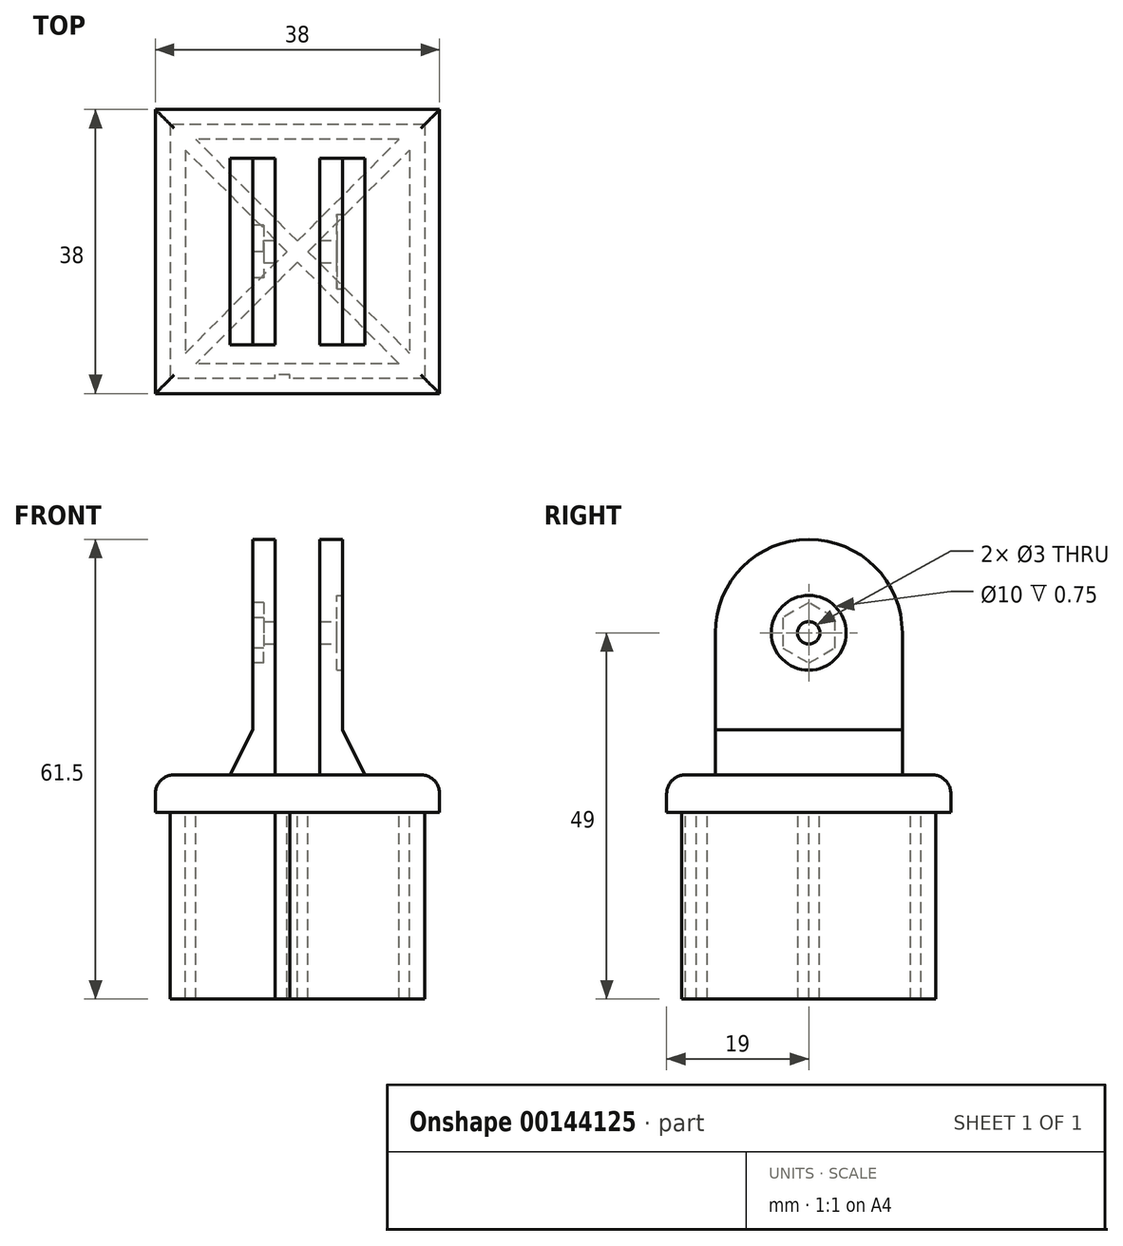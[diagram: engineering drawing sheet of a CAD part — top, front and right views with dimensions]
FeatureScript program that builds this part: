
annotation { "Feature Type Name" : "Feature", "Feature Type Description" : "" }
export const myFeature = defineFeature(function(context is Context, id is Id, definition is map)
    precondition{}
    {
        {
            var Q0;
            Q0=qCreatedBy(makeId("Top.planeOp"),FACE);
            var sketch = newSketch(context, id + "F0", { "sketchPlane" : qUnion([Q0])});
            skLineSegment(sketch, "E0.bottom", {"start": v(17, 17) * mm, "end": v(-17, 17) * mm});
            skLineSegment(sketch, "E0.top", {"start": v(17, -17) * mm, "end": v(-17, -17) * mm});
            skLineSegment(sketch, "E0.left", {"start": v(17, 17) * mm, "end": v(17, -17) * mm});
            skLineSegment(sketch, "E0.right", {"start": v(-17, 17) * mm, "end": v(-17, -17) * mm});
            skPoint(sketch, "E0.middle", {"position": v(0, 0) * mm});
            skLineSegment(sketch, "E1.bottom", {"start": v(19, 19) * mm, "end": v(-19, 19) * mm});
            skLineSegment(sketch, "E1.top", {"start": v(19, -19) * mm, "end": v(-19, -19) * mm});
            skLineSegment(sketch, "E1.left", {"start": v(19, 19) * mm, "end": v(19, -19) * mm});
            skLineSegment(sketch, "E1.right", {"start": v(-19, 19) * mm, "end": v(-19, -19) * mm});
            skLineSegment(sketch, "E2.bottom", {"start": v(15, 15) * mm, "end": v(-15, 15) * mm});
            skLineSegment(sketch, "E2.top", {"start": v(15, -15) * mm, "end": v(-15, -15) * mm});
            skLineSegment(sketch, "E2.left", {"start": v(15, 15) * mm, "end": v(15, -15) * mm});
            skLineSegment(sketch, "E2.right", {"start": v(-15, 15) * mm, "end": v(-15, -15) * mm});
            skSolve(sketch);
        }
        {
            var Q0;
            Q0 = qSketchRegion(id + "F0", true);
            var Q1;
            Q1=makeQuery(id+"F0.imprint","IMPRINT",FACE,{"disambiguationData":[TD([[makeQuery(id+"F0.imprint","IMPRINT",EDGE,{"derivedFrom":sQuery(id+"F0.wireOp",EDGE,"E0.bottom")}),1.0]])]});
            var Q2;
            Q2=makeQuery(id+"F0.imprint","IMPRINT",FACE,{"disambiguationData":[TD([[makeQuery(id+"F0.imprint","IMPRINT",EDGE,{"derivedFrom":sQuery(id+"F0.wireOp",EDGE,"E2.bottom")}),1.0]])]});
            extrude(context, id + "F1", {"entities" : qUnion([Q0, Q1, Q2]), "depth" : 5 * mm});
        }
        {
            var Q0;
            Q0=makeQuery(id+"F0.imprint","IMPRINT",FACE,{"disambiguationData":[TD([[makeQuery(id+"F0.imprint","IMPRINT",EDGE,{"derivedFrom":sQuery(id+"F0.wireOp",EDGE,"E0.bottom")}),1.0]])]});
            extrude(context, id + "F2", {"entities" : qUnion([Q0]), "operationType" : NewBodyOperationType.ADD, "oppositeDirection" : true, "depth" : 25 * mm});
        }
        {
            var Q0;
            Q0=makeQuery(id+"F0.imprint","IMPRINT",FACE,{"disambiguationData":[TD([[makeQuery(id+"F0.imprint","IMPRINT",EDGE,{"derivedFrom":sQuery(id+"F0.wireOp",EDGE,"E2.bottom")}),1.0]])]});
            var sketch = newSketch(context, id + "F3", { "sketchPlane" : qUnion([Q0])});
            skPoint(sketch, "E3", {"position": v(-15, 15) * mm});
            skPoint(sketch, "E4", {"position": v(15, -15) * mm});
            skPoint(sketch, "E5", {"position": v(-15, -15) * mm});
            skPoint(sketch, "E6", {"position": v(15, 15) * mm});
            skLineSegment(sketch, "E7", {"start": v(0.7, 0.7) * mm, "end": v(-13.59, 15) * mm});
            skLineSegment(sketch, "E8", {"start": v(-13.59, 15) * mm, "end": v(-15, 15) * mm});
            skLineSegment(sketch, "E9", {"start": v(-0.7, -0.7) * mm, "end": v(-15, 13.59) * mm});
            skLineSegment(sketch, "E10", {"start": v(-15, 13.59) * mm, "end": v(-15, 15) * mm});
            skLineSegment(sketch, "E11", {"start": v(-0.7, -0.7) * mm, "end": v(13.59, -15) * mm});
            skLineSegment(sketch, "E12", {"start": v(13.59, -15) * mm, "end": v(15, -15) * mm});
            skLineSegment(sketch, "E13", {"start": v(0.7, 0.7) * mm, "end": v(15, -13.59) * mm});
            skLineSegment(sketch, "E14", {"start": v(15, -13.59) * mm, "end": v(15, -15) * mm});
            skLineSegment(sketch, "E15", {"start": v(0, -1.41) * mm, "end": v(-13.59, -15) * mm});
            skLineSegment(sketch, "E16", {"start": v(-13.59, -15) * mm, "end": v(-15, -15) * mm});
            skLineSegment(sketch, "E17", {"start": v(-15, -13.59) * mm, "end": v(-1.41, 0) * mm});
            skLineSegment(sketch, "E18", {"start": v(1.41, 0) * mm, "end": v(15, 13.59) * mm});
            skLineSegment(sketch, "E19", {"start": v(15, 13.59) * mm, "end": v(15, 15) * mm});
            skLineSegment(sketch, "E20", {"start": v(0.7, 0.7) * mm, "end": v(0, 1.41) * mm});
            skLineSegment(sketch, "E21", {"start": v(0, 1.41) * mm, "end": v(13.59, 15) * mm});
            skLineSegment(sketch, "E22", {"start": v(13.59, 15) * mm, "end": v(15, 15) * mm});
            skSolve(sketch);
        }
        {
            var Q0;
            Q0 = qSketchRegion(id + "F3", true);
            extrude(context, id + "F4", {"entities" : qUnion([Q0]), "operationType" : NewBodyOperationType.ADD, "oppositeDirection" : true, "depth" : 25 * mm});
        }
        {
            var Q0;
            {var subQ0=sQuery(id+"F3.wireOp",EDGE,"E15");Q0=makeQuery(id+"F3.imprint","IMPRINT",FACE,{"disambiguationData":[TD([[makeQuery(id+"F3.imprint","IMPRINT",EDGE,{"derivedFrom":subQ0}),-1.0]])]});}
            extrude(context, id + "F5", {"entities" : qUnion([Q0]), "operationType" : NewBodyOperationType.ADD, "oppositeDirection" : true, "depth" : 25 * mm});
        }
        {
            var Q0;
            Q0=makeQuery(id+"F1.opExtrude","CAP_EDGE",EDGE,{"disambiguationData":[OSD([sQuery(id+"F0.wireOp",EDGE,"E1.bottom")])],"isStart":false});
            var Q1;
            Q1=makeQuery(id+"F1.opExtrude","CAP_EDGE",EDGE,{"disambiguationData":[OSD([sQuery(id+"F0.wireOp",EDGE,"E1.left")])],"isStart":false});
            var Q2;
            Q2=makeQuery(id+"F1.opExtrude","CAP_EDGE",EDGE,{"disambiguationData":[OSD([sQuery(id+"F0.wireOp",EDGE,"E1.right")])],"isStart":false});
            var Q3;
            Q3=makeQuery(id+"F1.opExtrude","CAP_EDGE",EDGE,{"disambiguationData":[OSD([sQuery(id+"F0.wireOp",EDGE,"E1.top")])],"isStart":false});
            fillet(context, id + "F6", {"entities" : qUnion([Q0, Q1, Q2, Q3]), "radius" : 2.5 * mm, "tangentPropagation" : true, "allowEdgeOverflow" : false});
        }
        {
            var Q0;
            Q0=makeQuery(id+"F1.opExtrude","CAP_FACE",FACE,{"disambiguationData":[OSD([sQuery(id+"F0.wireOp",EDGE,"E1.bottom"),sQuery(id+"F0.wireOp",EDGE,"E1.top"),sQuery(id+"F0.wireOp",EDGE,"E1.left"),sQuery(id+"F0.wireOp",EDGE,"E1.right")])],"isStart":false});
            var sketch = newSketch(context, id + "F7", { "sketchPlane" : qUnion([Q0])});
            skLineSegment(sketch, "E23.bottom", {"start": v(3, 12.5) * mm, "end": v(-3, 12.5) * mm});
            skLineSegment(sketch, "E23.top", {"start": v(3, -12.5) * mm, "end": v(-3, -12.5) * mm});
            skLineSegment(sketch, "E23.left", {"start": v(3, 12.5) * mm, "end": v(3, -12.5) * mm});
            skLineSegment(sketch, "E23.right", {"start": v(-3, 12.5) * mm, "end": v(-3, -12.5) * mm});
            skPoint(sketch, "E23.middle", {"position": v(0, 0) * mm});
            skLineSegment(sketch, "E24.bottom", {"start": v(3, 12.5) * mm, "end": v(6, 12.5) * mm});
            skLineSegment(sketch, "E24.top", {"start": v(3, -12.5) * mm, "end": v(6, -12.5) * mm});
            skLineSegment(sketch, "E24.right", {"start": v(6, 12.5) * mm, "end": v(6, -12.5) * mm});
            skLineSegment(sketch, "E25.bottom", {"start": v(-3, 12.5) * mm, "end": v(-6, 12.5) * mm});
            skLineSegment(sketch, "E25.top", {"start": v(-3, -12.5) * mm, "end": v(-6, -12.5) * mm});
            skLineSegment(sketch, "E25.right", {"start": v(-6, 12.5) * mm, "end": v(-6, -12.5) * mm});
            skLineSegment(sketch, "E26.bottom", {"start": v(6, 12.5) * mm, "end": v(9, 12.5) * mm});
            skLineSegment(sketch, "E26.top", {"start": v(6, -12.5) * mm, "end": v(9, -12.5) * mm});
            skLineSegment(sketch, "E26.right", {"start": v(9, 12.5) * mm, "end": v(9, -12.5) * mm});
            skLineSegment(sketch, "E27.bottom", {"start": v(-6, 12.5) * mm, "end": v(-9, 12.5) * mm});
            skLineSegment(sketch, "E27.top", {"start": v(-6, -12.5) * mm, "end": v(-9, -12.5) * mm});
            skLineSegment(sketch, "E27.right", {"start": v(-9, 12.5) * mm, "end": v(-9, -12.5) * mm});
            skSolve(sketch);
        }
        {
            var Q0;
            Q0=makeQuery(id+"F7.imprint","IMPRINT",FACE,{"disambiguationData":[TD([[makeQuery(id+"F7.imprint","IMPRINT",EDGE,{"derivedFrom":sQuery(id+"F7.wireOp",EDGE,"E25.bottom")}),1.0]])]});
            extrude(context, id + "F8", {"entities" : qUnion([Q0]), "operationType" : NewBodyOperationType.ADD, "depth" : 19 * mm});
        }
        {
            var Q0;
            Q0=makeQuery(id+"F7.imprint","IMPRINT",FACE,{"disambiguationData":[TD([[makeQuery(id+"F7.imprint","IMPRINT",EDGE,{"derivedFrom":sQuery(id+"F7.wireOp",EDGE,"E24.bottom")}),-1.0]])]});
            extrude(context, id + "F9", {"entities" : qUnion([Q0]), "operationType" : NewBodyOperationType.ADD, "depth" : 19 * mm});
        }
        {
            var Q0;
            Q0=makeQuery(id+"F7.imprint","IMPRINT",FACE,{"disambiguationData":[TD([[makeQuery(id+"F7.imprint","IMPRINT",EDGE,{"derivedFrom":sQuery(id+"F7.wireOp",EDGE,"E27.bottom")}),1.0]])]});
            var Q1;
            Q1=makeQuery(id+"F7.imprint","IMPRINT",FACE,{"disambiguationData":[TD([[makeQuery(id+"F7.imprint","IMPRINT",EDGE,{"derivedFrom":sQuery(id+"F7.wireOp",EDGE,"E26.bottom")}),-1.0]])]});
            extrude(context, id + "F10", {"entities" : qUnion([Q0, Q1]), "operationType" : NewBodyOperationType.ADD, "depth" : 6 * mm});
        }
        {
            var Q0;
            Q0=makeQuery(id+"F10.opExtrude","CAP_EDGE",EDGE,{"disambiguationData":[OSD([sQuery(id+"F7.wireOp",EDGE,"E27.right")])],"isStart":false});
            chamfer(context, id + "F11", {"entities" : qUnion([Q0]), "chamferType" : ChamferType.TWO_OFFSETS, "width1" : 3 * mm, "oppositeDirection" : false, "width2" : 6 * mm, "tangentPropagation" : true});
        }
        {
            var Q0;
            Q0=makeQuery(id+"F10.opExtrude","CAP_EDGE",EDGE,{"disambiguationData":[OSD([sQuery(id+"F7.wireOp",EDGE,"E26.right")])],"isStart":false});
            chamfer(context, id + "F12", {"entities" : qUnion([Q0]), "chamferType" : ChamferType.TWO_OFFSETS, "width1" : 6 * mm, "oppositeDirection" : false, "width2" : 3 * mm, "tangentPropagation" : true});
        }
        {
            var Q0;
            Q0=makeQuery(id+"F9.opExtrude","SWEPT_FACE",FACE,{"disambiguationData":[OSD([sQuery(id+"F7.wireOp",EDGE,"E24.right")])]});
            var sketch = newSketch(context, id + "F13", { "sketchPlane" : qUnion([Q0])});
            skCircle(sketch, "E28", {"center": v(0, 24) * mm, "radius": 12.5 * mm});
            skCircle(sketch, "E29", {"center": v(0, 24) * mm, "radius": 5 * mm});
            skCircle(sketch, "E30", {"center": v(0, 24) * mm, "radius": 1.5 * mm});
            skSolve(sketch);
        }
        {
            var Q0;
            {var subQ1=sQuery(id+"F7.wireOp",EDGE,"E24.right");var subQ2=makeQuery(id+"F9.opExtrude","CAP_EDGE",EDGE,{"disambiguationData":[OSD([subQ1])],"isStart":false});var subQ5=sQuery(id+"F13.wireOp",EDGE,"E29");var subQ6=makeQuery(id+"F13.imprint","INTERSECT",VERTEX,{"disambiguationData":[OD(0.0)],"derivedFrom":[subQ2,subQ5]});Q0=makeQuery(id+"F13.imprint","IMPRINT",FACE,{"disambiguationData":[TD([[makeQuery(id+"F13.imprint","IMPRINT",EDGE,{"disambiguationData":[TD([[subQ6,1.0]])],"derivedFrom":subQ5}),-1.0]])]});}
            var Q1;
            {var subQ1=sQuery(id+"F7.wireOp",EDGE,"E24.right");var subQ2=makeQuery(id+"F9.opExtrude","CAP_EDGE",EDGE,{"disambiguationData":[OSD([subQ1])],"isStart":false});var subQ5=sQuery(id+"F13.wireOp",EDGE,"E29");var subQ6=makeQuery(id+"F13.imprint","INTERSECT",VERTEX,{"disambiguationData":[OD(0.0)],"derivedFrom":[subQ2,subQ5]});Q1=makeQuery(id+"F13.imprint","IMPRINT",FACE,{"disambiguationData":[TD([[makeQuery(id+"F13.imprint","IMPRINT",EDGE,{"disambiguationData":[TD([[subQ6,-1.0]])],"derivedFrom":subQ5}),-1.0]])]});}
            var Q2;
            {var subQ0=sQuery(id+"F13.wireOp",EDGE,"E29");var subQ1=makeQuery(id+"F9.opExtrude","CAP_EDGE",EDGE,{"disambiguationData":[OSD([sQuery(id+"F7.wireOp",EDGE,"E24.right")])],"isStart":false});var subQ2=makeQuery(id+"F13.imprint","INTERSECT",VERTEX,{"disambiguationData":[OD(0.0)],"derivedFrom":[subQ1,subQ0]});Q2=makeQuery(id+"F13.imprint","IMPRINT",FACE,{"disambiguationData":[TD([[makeQuery(id+"F13.imprint","IMPRINT",EDGE,{"disambiguationData":[TD([[subQ2,-1.0]])],"derivedFrom":subQ0}),1.0]])]});}
            var Q3;
            {var subQ0=sQuery(id+"F13.wireOp",EDGE,"E30");var subQ1=makeQuery(id+"F9.opExtrude","CAP_EDGE",EDGE,{"disambiguationData":[OSD([sQuery(id+"F7.wireOp",EDGE,"E24.right")])],"isStart":false});var subQ2=makeQuery(id+"F13.imprint","INTERSECT",VERTEX,{"disambiguationData":[OD(0.0)],"derivedFrom":[subQ1,subQ0]});Q3=makeQuery(id+"F13.imprint","IMPRINT",FACE,{"disambiguationData":[TD([[makeQuery(id+"F13.imprint","IMPRINT",EDGE,{"disambiguationData":[TD([[subQ2,-1.0]])],"derivedFrom":subQ0}),1.0]])]});}
            extrude(context, id + "F14", {"entities" : qUnion([Q0, Q1, Q2, Q3]), "operationType" : NewBodyOperationType.ADD, "oppositeDirection" : true, "depth" : 3 * mm});
        }
        {
            var Q0;
            Q0=makeQuery(id+"F8.opExtrude","SWEPT_FACE",FACE,{"disambiguationData":[OSD([sQuery(id+"F7.wireOp",EDGE,"E25.right")])]});
            var sketch = newSketch(context, id + "F15", { "sketchPlane" : qUnion([Q0])});
            skCircle(sketch, "E31", {"center": v(0, 24) * mm, "radius": 12.5 * mm});
            skCircle(sketch, "E32", {"center": v(0, 24) * mm, "radius": 1.5 * mm});
            skLineSegment(sketch, "E33.0", {"start": v(3.5, 26.02) * mm, "end": v(3.5, 21.98) * mm});
            skLineSegment(sketch, "E33.1", {"start": v(3.5, 21.98) * mm, "end": v(0, 19.96) * mm});
            skLineSegment(sketch, "E33.2", {"start": v(0, 19.96) * mm, "end": v(-3.5, 21.98) * mm});
            skLineSegment(sketch, "E33.3", {"start": v(-3.5, 21.98) * mm, "end": v(-3.5, 26.02) * mm});
            skLineSegment(sketch, "E33.4", {"start": v(-3.5, 26.02) * mm, "end": v(0, 28.04) * mm});
            skLineSegment(sketch, "E33.5", {"start": v(0, 28.04) * mm, "end": v(3.5, 26.02) * mm});
            skPoint(sketch, "E33.0.midPoint", {"position": v(3.5, 24) * mm});
            skSolve(sketch);
        }
        {
            var Q0;
            {var subQ1=sQuery(id+"F7.wireOp",EDGE,"E25.right");var subQ2=makeQuery(id+"F8.opExtrude","CAP_EDGE",EDGE,{"disambiguationData":[OSD([subQ1])],"isStart":false});var subQ5=sQuery(id+"F15.wireOp",EDGE,"49741782-3f8c-4f9b-8aee-8919342bdeed");var subQ6=makeQuery(id+"F15.imprint","INTERSECT",VERTEX,{"disambiguationData":[OD(0.0)],"derivedFrom":[subQ2,subQ5]});Q0=makeQuery(id+"F15.imprint","IMPRINT",FACE,{"disambiguationData":[TD([[makeQuery(id+"F15.imprint","IMPRINT",EDGE,{"disambiguationData":[TD([[subQ6,1.0]])],"derivedFrom":subQ5}),-1.0]])]});}
            var Q1;
            {var subQ0=sQuery(id+"F15.wireOp",EDGE,"49741782-3f8c-4f9b-8aee-8919342bdeed");var subQ1=makeQuery(id+"F8.opExtrude","CAP_EDGE",EDGE,{"disambiguationData":[OSD([sQuery(id+"F7.wireOp",EDGE,"E25.right")])],"isStart":false});var subQ2=makeQuery(id+"F15.imprint","INTERSECT",VERTEX,{"disambiguationData":[OD(0.0)],"derivedFrom":[subQ1,subQ0]});Q1=makeQuery(id+"F15.imprint","IMPRINT",FACE,{"disambiguationData":[TD([[makeQuery(id+"F15.imprint","IMPRINT",EDGE,{"disambiguationData":[TD([[subQ2,1.0]])],"derivedFrom":subQ0}),1.0]])]});}
            var Q2;
            {var subQ0=sQuery(id+"F15.wireOp",EDGE,"E32");var subQ1=makeQuery(id+"F8.opExtrude","CAP_EDGE",EDGE,{"disambiguationData":[OSD([sQuery(id+"F7.wireOp",EDGE,"E25.right")])],"isStart":false});var subQ2=makeQuery(id+"F15.imprint","INTERSECT",VERTEX,{"disambiguationData":[OD(0.0)],"derivedFrom":[subQ1,subQ0]});Q2=makeQuery(id+"F15.imprint","IMPRINT",FACE,{"disambiguationData":[TD([[makeQuery(id+"F15.imprint","IMPRINT",EDGE,{"disambiguationData":[TD([[subQ2,1.0]])],"derivedFrom":subQ0}),1.0]])]});}
            extrude(context, id + "F16", {"entities" : qUnion([Q0, Q1, Q2]), "operationType" : NewBodyOperationType.ADD, "oppositeDirection" : true, "depth" : 3 * mm});
        }
        {
            var Q0;
            Q0=sQuery(id+"F13.wireOp",VERTEX,"E28.center");
            var Q1;
            Q1=makeQuery(id+"F1.opExtrude","SWEPT_BODY",BODY,{"disambiguationData":[OSD([sQuery(id+"F0.wireOp",EDGE,"E1.bottom"),sQuery(id+"F0.wireOp",EDGE,"E1.top"),sQuery(id+"F0.wireOp",EDGE,"E1.left"),sQuery(id+"F0.wireOp",EDGE,"E1.right")])]});
            hole(context, id + "F17", {"style" : HoleStyle.SIMPLE, "endStyle" : HoleEndStyle.THROUGH, "holeDiameter" : 3 * mm, "locations" : qUnion([Q0]), "scope" : qUnion([Q1]), "isTappedThrough" : true});
        }
        {
            var Q0;
            {var subQ0=sQuery(id+"F13.wireOp",EDGE,"E29");var subQ1=makeQuery(id+"F9.opExtrude","CAP_EDGE",EDGE,{"disambiguationData":[OSD([sQuery(id+"F7.wireOp",EDGE,"E24.right")])],"isStart":false});var subQ2=makeQuery(id+"F13.imprint","INTERSECT",VERTEX,{"disambiguationData":[OD(0.0)],"derivedFrom":[subQ1,subQ0]});Q0=makeQuery(id+"F13.imprint","IMPRINT",FACE,{"disambiguationData":[TD([[makeQuery(id+"F13.imprint","IMPRINT",EDGE,{"disambiguationData":[TD([[subQ2,1.0]])],"derivedFrom":subQ0}),1.0]])]});}
            var Q1;
            {var subQ0=sQuery(id+"F13.wireOp",EDGE,"E29");var subQ1=makeQuery(id+"F9.opExtrude","CAP_EDGE",EDGE,{"disambiguationData":[OSD([sQuery(id+"F7.wireOp",EDGE,"E24.right")])],"isStart":false});var subQ2=makeQuery(id+"F13.imprint","INTERSECT",VERTEX,{"disambiguationData":[OD(0.0)],"derivedFrom":[subQ1,subQ0]});Q1=makeQuery(id+"F13.imprint","IMPRINT",FACE,{"disambiguationData":[TD([[makeQuery(id+"F13.imprint","IMPRINT",EDGE,{"disambiguationData":[TD([[subQ2,-1.0]])],"derivedFrom":subQ0}),1.0]])]});}
            extrude(context, id + "F18", {"entities" : qUnion([Q0, Q1]), "operationType" : NewBodyOperationType.REMOVE, "endBound" : BoundingType.SYMMETRIC, "oppositeDirection" : true, "depth" : 1.5 * mm});
        }
        {
            var Q0;
            {var subQ0=sQuery(id+"F15.wireOp",EDGE,"E33.4");Q0=makeQuery(id+"F15.imprint","IMPRINT",FACE,{"disambiguationData":[TD([[makeQuery(id+"F15.imprint","IMPRINT",EDGE,{"derivedFrom":subQ0}),1.0]])]});}
            var Q1;
            {var subQ0=sQuery(id+"F15.wireOp",EDGE,"E33.4");Q1=makeQuery(id+"F15.imprint","IMPRINT",FACE,{"disambiguationData":[TD([[makeQuery(id+"F15.imprint","IMPRINT",EDGE,{"derivedFrom":subQ0}),-1.0]])]});}
            extrude(context, id + "F19", {"entities" : qUnion([Q0, Q1]), "operationType" : NewBodyOperationType.ADD, "oppositeDirection" : true, "depth" : 3 * mm});
        }
        {
            var Q0;
            {var subQ0=sQuery(id+"F15.wireOp",EDGE,"E33.4");Q0=makeQuery(id+"F15.imprint","IMPRINT",FACE,{"disambiguationData":[TD([[makeQuery(id+"F15.imprint","IMPRINT",EDGE,{"derivedFrom":subQ0}),-1.0]])]});}
            var Q1;
            {var subQ1=sQuery(id+"F15.wireOp",EDGE,"E33.1");Q1=makeQuery(id+"F15.imprint","IMPRINT",FACE,{"disambiguationData":[TD([[makeQuery(id+"F15.imprint","IMPRINT",EDGE,{"derivedFrom":subQ1}),-1.0]])]});}
            extrude(context, id + "F20", {"entities" : qUnion([Q0, Q1]), "operationType" : NewBodyOperationType.REMOVE, "oppositeDirection" : true, "depth" : 1.5 * mm});
        }
        {
            var Q0;
            Q0=makeQuery(id+"F2.opExtrude","SWEPT_FACE",FACE,{"disambiguationData":[OSD([sQuery(id+"F0.wireOp",EDGE,"E0.top")])]});
            var sketch = newSketch(context, id + "F21", { "sketchPlane" : qUnion([Q0])});
            skLineSegment(sketch, "E34", {"start": v(-3, -25) * mm, "end": v(-3, 0) * mm});
            skLineSegment(sketch, "E35", {"start": v(-3, 0) * mm, "end": v(-1, 0) * mm});
            skLineSegment(sketch, "E36", {"start": v(-1, 0) * mm, "end": v(-1, -25) * mm});
            skPoint(sketch, "E36.endSnap0", {"position": v(0, -25) * mm});
            skLineSegment(sketch, "E37", {"start": v(-1, -25) * mm, "end": v(-3, -25) * mm});
            skSolve(sketch);
        }
        {
            var Q0;
            Q0=makeQuery(id+"F21.imprint","IMPRINT",FACE,{"disambiguationData":[TD([[makeQuery(id+"F21.imprint","IMPRINT",EDGE,{"derivedFrom":sQuery(id+"F21.wireOp",EDGE,"E34")}),-1.0]])]});
            extrude(context, id + "F22", {"entities" : qUnion([Q0]), "operationType" : NewBodyOperationType.REMOVE, "endBound" : BoundingType.SYMMETRIC, "depth" : 1 * mm});
        }
    });
